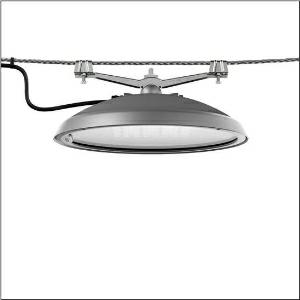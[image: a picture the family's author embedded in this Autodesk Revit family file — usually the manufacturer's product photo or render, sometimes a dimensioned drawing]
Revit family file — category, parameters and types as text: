
# Revit family: dl_r__50_iq_mini___st1_0s_5xa248w31f08re_8883
name_source: partatom
category: Lighting Fixtures
units: mm (PartAtom-declared; Revit-internal decimal feet)

## family parameters
Cut with Voids When Loaded = No
Host = Face
Light Source = No
Part Type = Normal
Room Calculation Point = No
Round Connector Dimension = Use Diameter
Shared = No

## types (1)
- --- (1 x LED, 6000 lm, 35.4 W, 3000K)
    Apparent Load = 35 VA
    CIE Flux Codes = 37 72 97 100 100
    Color Rendering = 70
    Color Temperature = 3000K
    Default Elevation = 1800 mm
    Description = DL® 50 iQ mini, catenary luminaire, primary light control with lens, of PMMA, primary optical cover: cover, of toughened safety glass, transparent, light distribution: ST1.0s, light emission: direct distribution, primary light characteristic: symmetric, installation type: suspended mounting, LED, High Power LED, rated luminous flux: 6.000lm, luminous efficacy: 170lm/W, light colour: 730, colour temperature: 3000K, control gear: iQ Street-Remote, control: optimised constant luminous flux control (CLO 2.0), Desk-Remote (wireless, voltage-free reading and setting of iQ features in the workshop via application-optimized NFC function/RFID function), Light-Fading, Smart-Wire, Night-Set, Lumen-Switch, Temp-Guard, Auto-Match, Street-Remote, mains connection: 230..240V, AC, 50/60Hz, start of lifetime: 35W, end of service life: 36W, reduction: 17W, luminaire housing, of diecast aluminium, powder-coated, Siteco® metallic grey (DB 702S), diameter: 500mm, height: 115mm, mounting height: 4..12m, protection rating (complete): IP66, insulation class (complete): insulation class II (safety insulation), certification: CE, ENEC, ENEC+, VDE, impact resistance: IK08, permissible operating ambient temperature for outdoor applications: -25..+40°C, standard-compliant lighting for roads and squares, packaging unit: 1 piece

Light Distribution: ST1.0s
    Height = 124 mm  [stored 0.406824 ft]
    Lamp = 1 x LED
    Lamp Light Flux = 6000 lm
    Lamp Power = 35.4 W
    Lamp count = 1
    Length = 500 mm
    Luminous efficacy = 169 lm/W
    Manufacturer = Siteco
    ModVariant = No
    Model = 5XA248W31F08RE
    Number of Poles = 1
    OnlyDefault = Yes
    Power Factor = 1
    Product Name = DL® 50 iQ mini | ST1.0s
    Product group = catenary luminaire
    ProductGroupID = 6300
    Protection Class = Protection class II
    Protection Degree = IP 66
    RLX_Detail_Level = 1
    RLX_Emergency_Light_Flux = 0 lm
    RLX_Emergency_Type = 0
    RLX_Emergency_Type_DB = No
    RlxData = <blob elided: 124189 chars, md5=c3f9699a>
    Socket = socket
    Standby Power = 0 W
    System Light Flux = 6000 lm
    System Power = 35 W
    Type Comments = factory setting: luminous flux: 100 % | dim-lin: 254 | 376 mA
    Type Image = l_1242791.jpg
    URL = http://relux.com
    VarID = @adj_162233
    Voltage = 0 V
    Weight = 0.00 kg
    Width = 0 mm  [stored 0 ft]

note: [stored X ft] marks values corroborated as IEEE doubles in the binary element streams (Revit-internal decimal feet)

## geometry (parser evidence)
native form markers: Blend x4, Sweep x14
no freeform markers — native parametric forms only
